# Revit family: PM4010001_Ducha regadera cuadrada Palma
name_source: partatom
category: Plumbing Fixtures
units: mm (PartAtom-declared; Revit-internal decimal feet)

## family parameters
Always vertical = Yes
Cut with Voids When Loaded = No
Host = Wall
OmniClass Number = 23.31.17.00
OmniClass Title = Showers
Part Type = Normal
Room Calculation Point = No
Round Connector Dimension = Use Diameter
Shared = No

## types (1)
- Ducha regadera cuadrada Palma
    Alto = 148 mm
    Ancho = 250 mm  [stored 0.82021 ft]
    Capacidad de flujo = A 80 psi: 8.4 L/min.
    Conexión de rosca = 1/2'' NPT
    Creado por = BIMBAU
    Default Elevation = 0 mm  [stored 0 ft]
    Description = La línea Palma cuenta con todos los atributos de diseño y funcionalidad que la hacen perfecta para soluciones en espacios actuales. Ofrece una línea de griferías para ducha, lavamanos y accesorios con la perfecta combinacion de líneas rectas y modernas.
    Dimensiones generales del producto = (Regadera): 200 x 250 mm.
    Diámetro abasto = 13 mm
    Fecha de creación = 07/05/2021
    Manufacturer = Corona.
    Material = Corona_Plastico_Cromado
    Material 2 = Corona_Plastico_Gris
    Material 3 = Corona_Acero inoxidable
    Model = PM4010001_Ducha regadera cuadrada Palma.
    Normatividad = NTC 1644.
    Peso neto = 601 gr. / 1.32 lb.
    Presión máxima recomendada = 125 psi (862 kPa).
    Presión mínima recomendada = 20 psi (138 kPa).
    Profundidad = 468 mm
    Recubrimientos = Resistente a la corrosión, pelado y decoloración por agua. Recubrimientos no tóxicos. Producto para uso doméstico.
    Temperatura de uso = 5° C a 71° C.
    Vida útil = 10000 ciclos.

note: [stored X ft] marks values corroborated as IEEE doubles in the binary element streams (Revit-internal decimal feet)

## geometry (parser evidence)
native form markers: Sweep x8
no freeform markers — native parametric forms only
